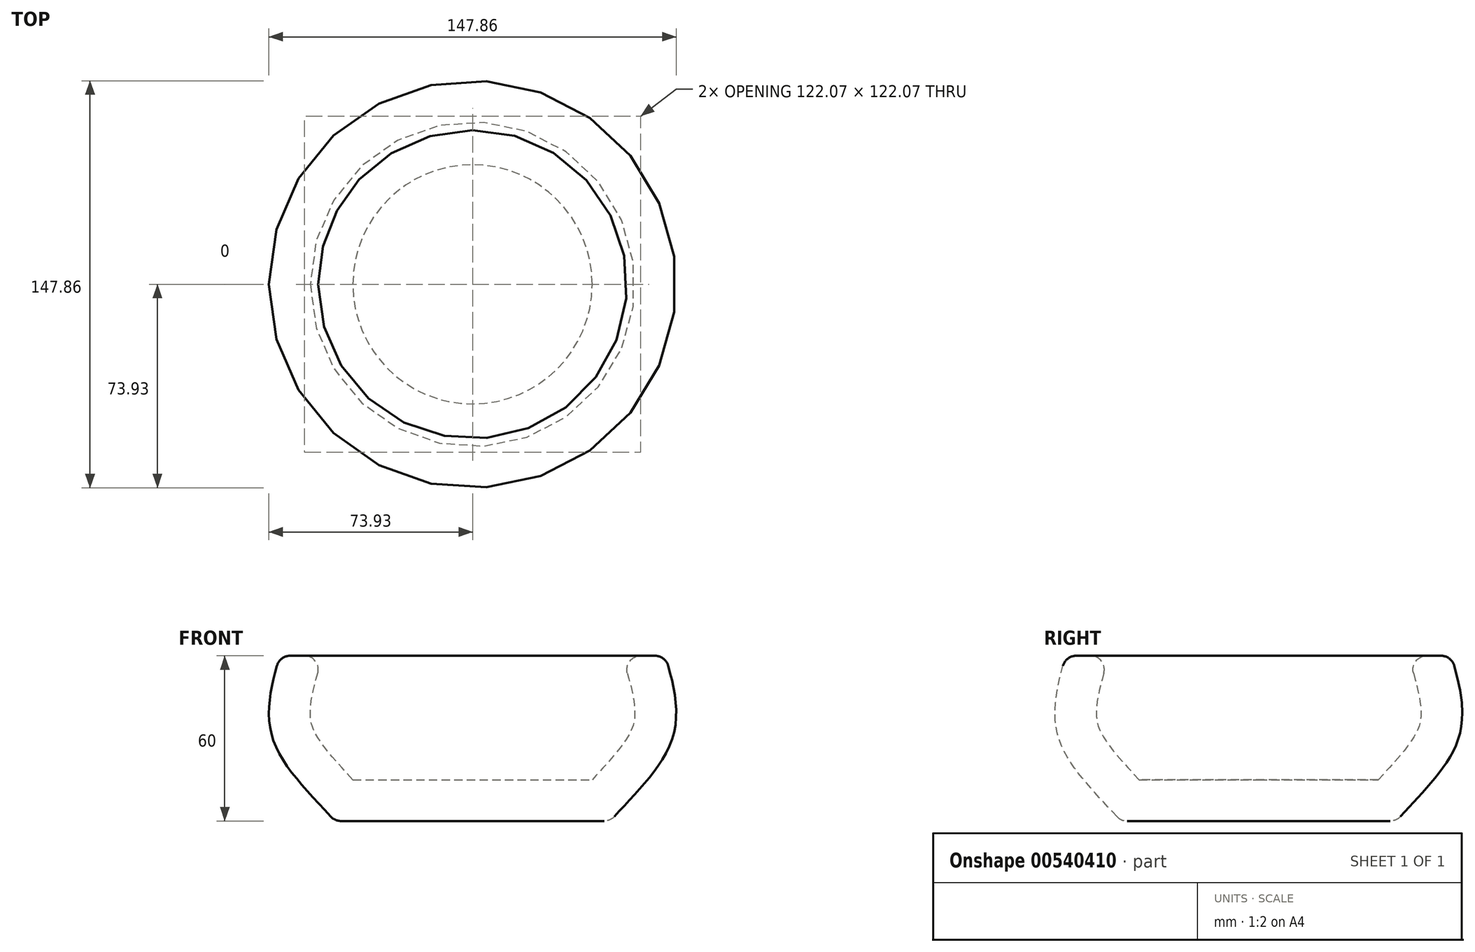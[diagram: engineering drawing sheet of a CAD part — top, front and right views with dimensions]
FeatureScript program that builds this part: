
annotation { "Feature Type Name" : "Feature", "Feature Type Description" : "" }
export const myFeature = defineFeature(function(context is Context, id is Id, definition is map)
    precondition{}
    {
        {
            var Q0;
            Q0=qCreatedBy(makeId("Front.planeOp"),FACE);
            var sketch = newSketch(context, id + "F0", { "sketchPlane" : qUnion([Q0])});
            skLineSegment(sketch, "E0", {"start": v(-70, 60) * mm, "end": v(0, 60) * mm});
            skLineSegment(sketch, "E1", {"start": v(0, 0) * mm, "end": v(-50, 0) * mm});
            skFitSpline(sketch, "E2", {"points": [v(-50, 0) * mm, v(-72.92, 31.18) * mm, v(-70, 60) * mm], "startDerivative": vector(-54.98, 60.24) * mm, "endDerivative": vector(17.34, 59.74) * mm});
            skLineSegment(sketch, "E3", {"start": v(0, 0) * mm, "end": v(0, 60) * mm});
            skSolve(sketch);
        }
        {
            var Q0;
            Q0=makeQuery(id+"F0.imprint","IMPRINT",FACE,{"disambiguationData":[TD([[makeQuery(id+"F0.imprint","IMPRINT",EDGE,{"derivedFrom":sQuery(id+"F0.wireOp",EDGE,"E0")}),-1.0]])]});
            var Q1;
            Q1=sQuery(id+"F0.wireOp",EDGE,"E3");
            revolve(context, id + "F1", {"entities" : qUnion([Q0]), "axis" : qUnion([Q1]), "revolveType" : RevolveType.FULL});
        }
        {
            var Q0;
            Q0=makeQuery(id+"F1.opRevolve","SWEPT_FACE",FACE,{"disambiguationData":[OSD([sQuery(id+"F0.wireOp",EDGE,"E0")])]});
            shell(context, id + "F2", {"entities" : qUnion([Q0]), "thickness" : 15 * mm});
        }
        {
            var Q0;
            Q0=makeQuery(id+"F1.opRevolve","SWEPT_EDGE",EDGE,{"disambiguationData":[OSD([sQuery(id+"F0.wireOp",EDGE,"E0"),sQuery(id+"F0.wireOp",EDGE,"E2")])]});
            var Q1;
            Q1=makeQuery(id+"F2.opShell","OFFSET_EDGE",EDGE,{"disambiguationData":[OSD([sQuery(id+"F0.wireOp",EDGE,"E0"),sQuery(id+"F0.wireOp",EDGE,"E2")])]});
            var Q2;
            Q2=makeQuery(id+"F1.opRevolve","SWEPT_EDGE",EDGE,{"disambiguationData":[OSD([sQuery(id+"F0.wireOp",EDGE,"E1"),sQuery(id+"F0.wireOp",EDGE,"E2")])]});
            fillet(context, id + "F3", {"entities" : qUnion([Q0, Q1, Q2]), "radius" : 5 * mm, "tangentPropagation" : true, "allowEdgeOverflow" : false});
        }
    });
